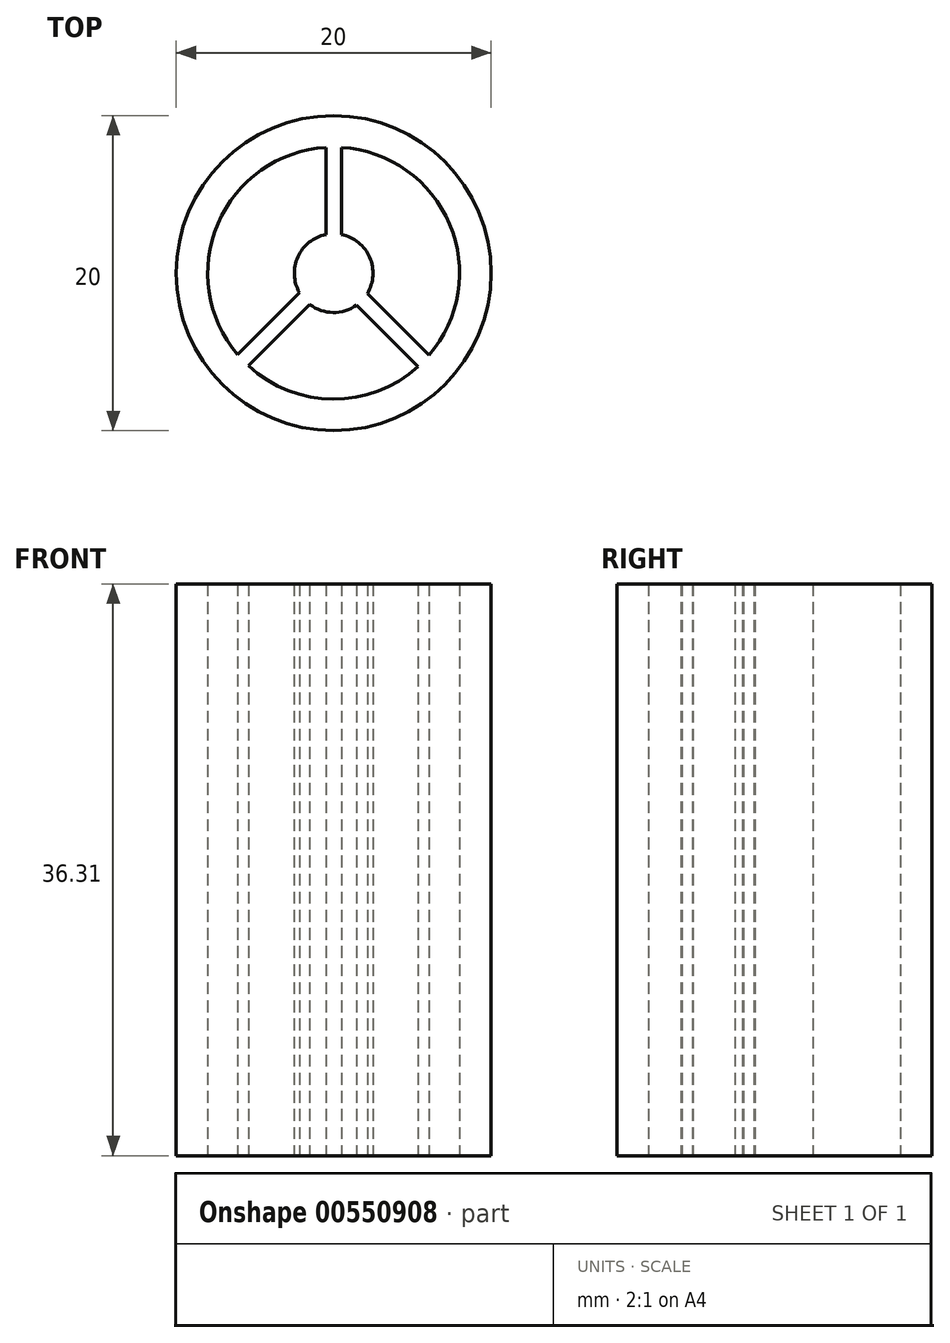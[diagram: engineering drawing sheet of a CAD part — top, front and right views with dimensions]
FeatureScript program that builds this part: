
annotation { "Feature Type Name" : "Feature", "Feature Type Description" : "" }
export const myFeature = defineFeature(function(context is Context, id is Id, definition is map)
    precondition{}
    {
        {
            var Q0;
            Q0=qCreatedBy(makeId("Top.planeOp"),FACE);
            var sketch = newSketch(context, id + "F0", { "sketchPlane" : qUnion([Q0])});
            skCircle(sketch, "E0", {"center": v(-18.96, 10.04) * mm, "radius": 10 * mm});
            skCircle(sketch, "E1", {"center": v(-18.96, 10.04) * mm, "radius": 2.5 * mm});
            skCircle(sketch, "E2", {"center": v(-18.96, 10.04) * mm, "radius": 8 * mm});
            skLineSegment(sketch, "E3.bottom", {"start": v(-19.46, 19.1) * mm, "end": v(-18.46, 19.1) * mm});
            skLineSegment(sketch, "E3.top", {"start": v(-19.46, 11.25) * mm, "end": v(-18.46, 11.25) * mm});
            skLineSegment(sketch, "E3.left", {"start": v(-19.46, 19.1) * mm, "end": v(-19.46, 11.25) * mm});
            skLineSegment(sketch, "E3.right", {"start": v(-18.46, 19.1) * mm, "end": v(-18.46, 11.25) * mm});
            skLineSegment(sketch, "E4.bottom", {"start": v(-12.1, 4.03) * mm, "end": v(-12.81, 3.32) * mm});
            skLineSegment(sketch, "E4.top", {"start": v(-17.55, 9.48) * mm, "end": v(-18.26, 8.77) * mm});
            skLineSegment(sketch, "E4.left", {"start": v(-12.1, 4.03) * mm, "end": v(-17.55, 9.48) * mm});
            skLineSegment(sketch, "E4.right", {"start": v(-12.81, 3.32) * mm, "end": v(-18.26, 8.77) * mm});
            skLineSegment(sketch, "E5.bottom", {"start": v(-25.38, 3.15) * mm, "end": v(-26.08, 3.86) * mm});
            skLineSegment(sketch, "E5.top", {"start": v(-19.79, 8.74) * mm, "end": v(-20.5, 9.45) * mm});
            skLineSegment(sketch, "E5.left", {"start": v(-25.38, 3.15) * mm, "end": v(-19.79, 8.74) * mm});
            skLineSegment(sketch, "E5.right", {"start": v(-26.08, 3.86) * mm, "end": v(-20.5, 9.45) * mm});
            skSolve(sketch);
        }
        {
            var Q0;
            Q0=makeQuery(id+"F0.imprint","IMPRINT",FACE,{"disambiguationData":[TD([[makeQuery(id+"F0.imprint","IMPRINT",EDGE,{"derivedFrom":sQuery(id+"F0.wireOp",EDGE,"E0")}),1.0]])]});
            var Q1;
            {var subQ0=sQuery(id+"F0.wireOp",EDGE,"E3.left");var subQ1=sQuery(id+"F0.wireOp",EDGE,"E1");var subQ2=makeQuery(id+"F0.imprint","INTERSECT",VERTEX,{"derivedFrom":[subQ1,subQ0]});Q1=makeQuery(id+"F0.imprint","IMPRINT",FACE,{"disambiguationData":[TD([[makeQuery(id+"F0.imprint","IMPRINT",EDGE,{"disambiguationData":[TD([[subQ2,1.0]])],"derivedFrom":subQ1}),-1.0]])]});}
            var Q2;
            {var subQ5=sQuery(id+"F0.wireOp",EDGE,"E3.bottom");Q2=makeQuery(id+"F0.imprint","IMPRINT",FACE,{"disambiguationData":[TD([[makeQuery(id+"F0.imprint","IMPRINT",EDGE,{"derivedFrom":subQ5}),-1.0]])]});}
            var Q3;
            {var subQ5=sQuery(id+"F0.wireOp",EDGE,"E3.top");Q3=makeQuery(id+"F0.imprint","IMPRINT",FACE,{"disambiguationData":[TD([[makeQuery(id+"F0.imprint","IMPRINT",EDGE,{"derivedFrom":subQ5}),1.0]])]});}
            var Q4;
            {var subQ3=sQuery(id+"F0.wireOp",EDGE,"E3.top");Q4=makeQuery(id+"F0.imprint","IMPRINT",FACE,{"disambiguationData":[TD([[makeQuery(id+"F0.imprint","IMPRINT",EDGE,{"derivedFrom":subQ3}),-1.0]])]});}
            var Q5;
            {var subQ5=sQuery(id+"F0.wireOp",EDGE,"E4.top");Q5=makeQuery(id+"F0.imprint","IMPRINT",FACE,{"disambiguationData":[TD([[makeQuery(id+"F0.imprint","IMPRINT",EDGE,{"derivedFrom":subQ5}),1.0]])]});}
            var Q6;
            {var subQ0=sQuery(id+"F0.wireOp",EDGE,"E5.right");var subQ1=sQuery(id+"F0.wireOp",EDGE,"E1");var subQ2=makeQuery(id+"F0.imprint","INTERSECT",VERTEX,{"derivedFrom":[subQ1,subQ0]});Q6=makeQuery(id+"F0.imprint","IMPRINT",FACE,{"disambiguationData":[TD([[makeQuery(id+"F0.imprint","IMPRINT",EDGE,{"disambiguationData":[TD([[subQ2,-1.0]])],"derivedFrom":subQ1}),-1.0]])]});}
            var Q7;
            {var subQ5=sQuery(id+"F0.wireOp",EDGE,"E5.top");Q7=makeQuery(id+"F0.imprint","IMPRINT",FACE,{"disambiguationData":[TD([[makeQuery(id+"F0.imprint","IMPRINT",EDGE,{"derivedFrom":subQ5}),1.0]])]});}
            var Q8;
            {var subQ5=sQuery(id+"F0.wireOp",EDGE,"E5.bottom");Q8=makeQuery(id+"F0.imprint","IMPRINT",FACE,{"disambiguationData":[TD([[makeQuery(id+"F0.imprint","IMPRINT",EDGE,{"derivedFrom":subQ5}),-1.0]])]});}
            var Q9;
            {var subQ0=sQuery(id+"F0.wireOp",EDGE,"E4.right");var subQ1=sQuery(id+"F0.wireOp",EDGE,"E1");var subQ2=makeQuery(id+"F0.imprint","INTERSECT",VERTEX,{"derivedFrom":[subQ1,subQ0]});Q9=makeQuery(id+"F0.imprint","IMPRINT",FACE,{"disambiguationData":[TD([[makeQuery(id+"F0.imprint","IMPRINT",EDGE,{"disambiguationData":[TD([[subQ2,-1.0]])],"derivedFrom":subQ1}),-1.0]])]});}
            var Q10;
            {var subQ5=sQuery(id+"F0.wireOp",EDGE,"E4.bottom");Q10=makeQuery(id+"F0.imprint","IMPRINT",FACE,{"disambiguationData":[TD([[makeQuery(id+"F0.imprint","IMPRINT",EDGE,{"derivedFrom":subQ5}),-1.0]])]});}
            extrude(context, id + "F1", {"entities" : qUnion([Q0, Q1, Q2, Q3, Q4, Q5, Q6, Q7, Q8, Q9, Q10]), "depth" : 36.3 * mm, "offsetDistance" : 25 * mm});
        }
    });
